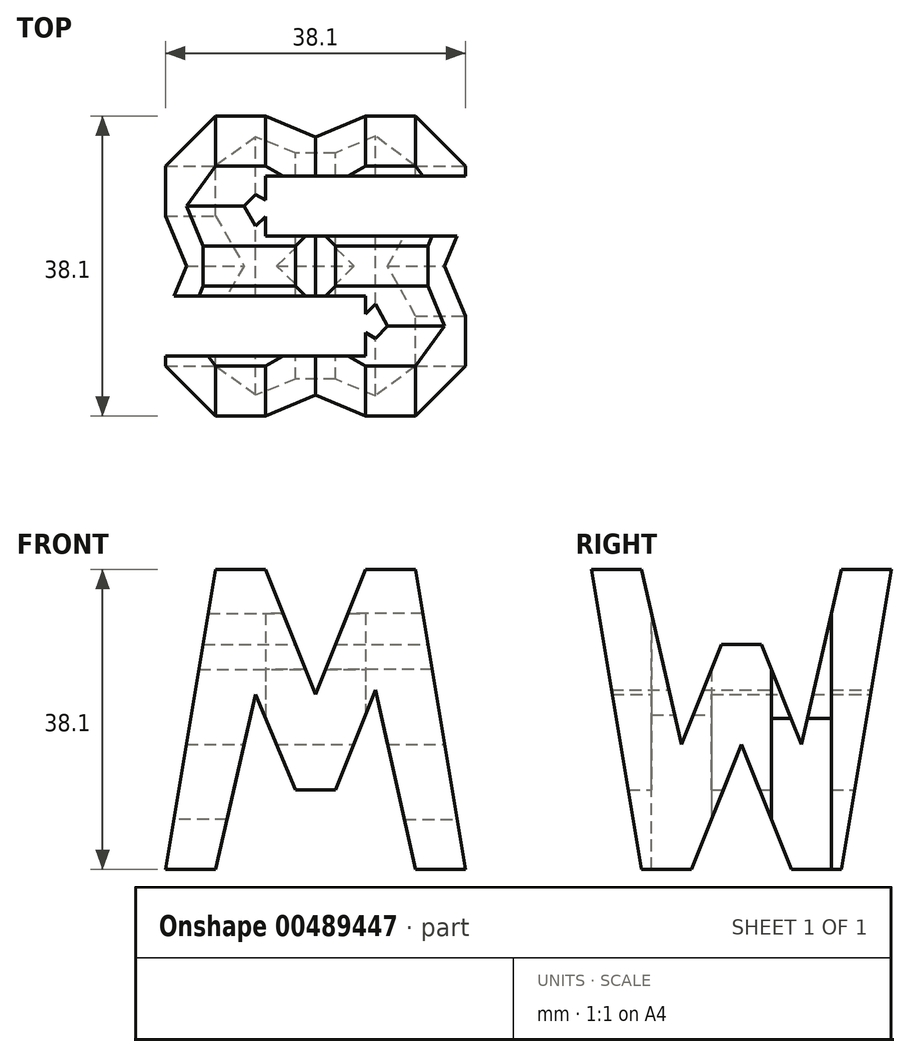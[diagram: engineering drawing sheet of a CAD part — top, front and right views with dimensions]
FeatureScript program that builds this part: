
annotation { "Feature Type Name" : "Feature", "Feature Type Description" : "" }
export const myFeature = defineFeature(function(context is Context, id is Id, definition is map)
    precondition{}
    {
        {
            var Q0;
            Q0=qCreatedBy(makeId("Front.planeOp"),FACE);
            var sketch = newSketch(context, id + "F0", { "sketchPlane" : qUnion([Q0])});
            skLineSegment(sketch, "E0", {"start": v(0, 0) * mm, "end": v(0, 38.1) * mm});
            skLineSegment(sketch, "E1", {"start": v(0, 0) * mm, "end": v(38.1, 0) * mm});
            skLineSegment(sketch, "E2", {"start": v(38.1, 0) * mm, "end": v(38.1, 38.1) * mm});
            skLineSegment(sketch, "E3", {"start": v(0, 38.1) * mm, "end": v(38.1, 38.1) * mm});
            skSolve(sketch);
        }
        {
            var Q0;
            Q0=makeQuery(id+"F0.imprint","IMPRINT",FACE,{"disambiguationData":[TD([[makeQuery(id+"F0.imprint","IMPRINT",EDGE,{"derivedFrom":sQuery(id+"F0.wireOp",EDGE,"E0")}),-1.0]])]});
            extrude(context, id + "F1", {"entities" : qUnion([Q0]), "depth" : 38.1 * mm, "offsetDistance" : 25.4 * mm});
        }
        {
            var Q0;
            Q0=qCreatedBy(makeId("Right.planeOp"),FACE);
            cPlane(context, id + "F2", {"entities" : qUnion([Q0]), "cplaneType" : CPlaneType.OFFSET, "offset" : 38.1 * mm, "width" : 152.4 * mm, "height" : 152.4 * mm});
        }
        {
            var Q0;
            Q0=qCreatedBy(id+"F2.planeOp",FACE);
            var sketch = newSketch(context, id + "F3", { "sketchPlane" : qUnion([Q0])});
            skLineSegment(sketch, "E4", {"start": v(-38.1, 38.1) * mm, "end": v(-38.1, 0) * mm});
            skLineSegment(sketch, "E5", {"start": v(-38.1, 0) * mm, "end": v(0, 0) * mm});
            skLineSegment(sketch, "E6", {"start": v(0, 0) * mm, "end": v(0, 38.1) * mm});
            skLineSegment(sketch, "E7", {"start": v(-38.1, 38.1) * mm, "end": v(0, 38.1) * mm});
            skLineSegment(sketch, "E8", {"start": v(-31.75, 38.1) * mm, "end": v(-26.67, 15.87) * mm});
            skLineSegment(sketch, "E9", {"start": v(-21.59, 28.58) * mm, "end": v(-16.5, 28.58) * mm});
            skLineSegment(sketch, "E10", {"start": v(-25.4, 0) * mm, "end": v(-19.05, 15.88) * mm});
            skLineSegment(sketch, "E11", {"start": v(-19.05, 15.88) * mm, "end": v(-12.7, 0) * mm});
            skLineSegment(sketch, "E12", {"start": v(-11.43, 15.88) * mm, "end": v(-6.35, 38.1) * mm});
            skLineSegment(sketch, "E13", {"start": v(-6.35, 0) * mm, "end": v(0, 38.1) * mm});
            skLineSegment(sketch, "E14", {"start": v(-31.75, 0) * mm, "end": v(-38.1, 38.1) * mm});
            skLineSegment(sketch, "E15", {"start": v(-11.43, 15.88) * mm, "end": v(-16.5, 28.58) * mm});
            skLineSegment(sketch, "E16", {"start": v(-21.59, 28.58) * mm, "end": v(-26.67, 15.87) * mm});
            skSolve(sketch);
        }
        {
            var Q0;
            {var subQ1=sQuery(id+"F3.wireOp",EDGE,"E8");Q0=makeQuery(id+"F3.imprint","IMPRINT",FACE,{"disambiguationData":[TD([[makeQuery(id+"F3.imprint","IMPRINT",EDGE,{"derivedFrom":subQ1}),1.0]])]});}
            var Q1;
            {var subQ0=sQuery(id+"F3.wireOp",EDGE,"E10");Q1=makeQuery(id+"F3.imprint","IMPRINT",FACE,{"disambiguationData":[TD([[makeQuery(id+"F3.imprint","IMPRINT",EDGE,{"derivedFrom":subQ0}),-1.0]])]});}
            var Q2;
            {var subQ0=sQuery(id+"F3.wireOp",EDGE,"E6");Q2=makeQuery(id+"F3.imprint","IMPRINT",FACE,{"disambiguationData":[TD([[makeQuery(id+"F3.imprint","IMPRINT",EDGE,{"derivedFrom":subQ0}),1.0]])]});}
            var Q3;
            {var subQ0=sQuery(id+"F3.wireOp",EDGE,"E4");Q3=makeQuery(id+"F3.imprint","IMPRINT",FACE,{"disambiguationData":[TD([[makeQuery(id+"F3.imprint","IMPRINT",EDGE,{"derivedFrom":subQ0}),1.0]])]});}
            extrude(context, id + "F4", {"entities" : qUnion([Q0, Q1, Q2, Q3]), "operationType" : NewBodyOperationType.REMOVE, "oppositeDirection" : true, "depth" : 38.1 * mm, "offsetDistance" : 25.4 * mm});
        }
        {
            var Q0;
            Q0=qCreatedBy(makeId("Front.planeOp"),FACE);
            var sketch = newSketch(context, id + "F5", { "sketchPlane" : qUnion([Q0])});
            skLineSegment(sketch, "E17", {"start": v(38.1, 38.1) * mm, "end": v(38.1, 0) * mm});
            skLineSegment(sketch, "E18", {"start": v(0, 0) * mm, "end": v(0, 38.1) * mm});
            skLineSegment(sketch, "E19", {"start": v(0, 0) * mm, "end": v(38.1, 0) * mm});
            skLineSegment(sketch, "E20", {"start": v(38.1, 38.1) * mm, "end": v(0, 38.1) * mm});
            skLineSegment(sketch, "E21", {"start": v(38.1, 0) * mm, "end": v(31.75, 38.1) * mm});
            skLineSegment(sketch, "E22", {"start": v(25.4, 38.1) * mm, "end": v(19.05, 22.23) * mm});
            skLineSegment(sketch, "E23", {"start": v(19.05, 22.23) * mm, "end": v(12.7, 38.1) * mm});
            skLineSegment(sketch, "E24", {"start": v(6.35, 38.1) * mm, "end": v(0, 0) * mm});
            skLineSegment(sketch, "E25", {"start": v(31.75, 0) * mm, "end": v(26.67, 22.78) * mm});
            skLineSegment(sketch, "E26", {"start": v(26.67, 22.78) * mm, "end": v(21.59, 10.08) * mm});
            skLineSegment(sketch, "E27", {"start": v(21.59, 10.08) * mm, "end": v(16.51, 10.08) * mm});
            skLineSegment(sketch, "E28", {"start": v(16.51, 10.08) * mm, "end": v(11.43, 22.23) * mm});
            skLineSegment(sketch, "E29", {"start": v(11.43, 22.23) * mm, "end": v(6.35, 0) * mm});
            skSolve(sketch);
        }
        {
            var Q0;
            {var subQ0=sQuery(id+"F5.wireOp",EDGE,"E17");Q0=makeQuery(id+"F5.imprint","IMPRINT",FACE,{"disambiguationData":[TD([[makeQuery(id+"F5.imprint","IMPRINT",EDGE,{"derivedFrom":subQ0}),-1.0]])]});}
            var Q1;
            {var subQ0=sQuery(id+"F5.wireOp",EDGE,"E25");Q1=makeQuery(id+"F5.imprint","IMPRINT",FACE,{"disambiguationData":[TD([[makeQuery(id+"F5.imprint","IMPRINT",EDGE,{"derivedFrom":subQ0}),1.0]])]});}
            var Q2;
            {var subQ0=sQuery(id+"F5.wireOp",EDGE,"E22");Q2=makeQuery(id+"F5.imprint","IMPRINT",FACE,{"disambiguationData":[TD([[makeQuery(id+"F5.imprint","IMPRINT",EDGE,{"derivedFrom":subQ0}),-1.0]])]});}
            var Q3;
            {var subQ0=sQuery(id+"F5.wireOp",EDGE,"E18");Q3=makeQuery(id+"F5.imprint","IMPRINT",FACE,{"disambiguationData":[TD([[makeQuery(id+"F5.imprint","IMPRINT",EDGE,{"derivedFrom":subQ0}),-1.0]])]});}
            extrude(context, id + "F6", {"entities" : qUnion([Q0, Q1, Q2, Q3]), "operationType" : NewBodyOperationType.REMOVE, "depth" : 38.1 * mm, "offsetDistance" : 25.4 * mm});
        }
        {
            var Q0;
            Q0=qCreatedBy(makeId("Top.planeOp"),FACE);
            var sketch = newSketch(context, id + "F7", { "sketchPlane" : qUnion([Q0])});
            skLineSegment(sketch, "E30", {"start": v(0, 0) * mm, "end": v(38.1, 0) * mm});
            skLineSegment(sketch, "E31", {"start": v(38.1, 0) * mm, "end": v(38.1, -38.1) * mm});
            skLineSegment(sketch, "E32", {"start": v(38.1, -38.1) * mm, "end": v(0, -38.1) * mm});
            skLineSegment(sketch, "E33", {"start": v(0, -38.1) * mm, "end": v(0, 0) * mm});
            skLineSegment(sketch, "E34", {"start": v(38.1, -7.62) * mm, "end": v(12.7, -7.62) * mm});
            skLineSegment(sketch, "E35", {"start": v(12.7, -7.62) * mm, "end": v(12.7, -15.24) * mm});
            skLineSegment(sketch, "E36", {"start": v(12.7, -15.24) * mm, "end": v(38.1, -15.24) * mm});
            skLineSegment(sketch, "E37", {"start": v(0, -30.48) * mm, "end": v(25.4, -30.48) * mm});
            skLineSegment(sketch, "E38", {"start": v(25.4, -30.48) * mm, "end": v(25.4, -22.86) * mm});
            skLineSegment(sketch, "E39", {"start": v(25.4, -22.86) * mm, "end": v(0, -22.86) * mm});
            skLineSegment(sketch, "E40", {"start": v(38.1, -15.24) * mm, "end": v(38.1, -7.62) * mm});
            skLineSegment(sketch, "E41", {"start": v(0, -30.48) * mm, "end": v(0, -22.86) * mm});
            skLineSegment(sketch, "E42", {"start": v(0, -38.1) * mm, "end": v(38.1, -38.1) * mm});
            skLineSegment(sketch, "E43", {"start": v(0, 0) * mm, "end": v(0, -38.1) * mm});
            skSolve(sketch);
        }
        {
            var Q0;
            {var subQ0=sQuery(id+"F7.wireOp",EDGE,"E34");Q0=makeQuery(id+"F7.imprint","IMPRINT",FACE,{"disambiguationData":[TD([[makeQuery(id+"F7.imprint","IMPRINT",EDGE,{"derivedFrom":subQ0}),1.0]])]});}
            var Q1;
            {var subQ0=sQuery(id+"F7.wireOp",EDGE,"E37");Q1=makeQuery(id+"F7.imprint","IMPRINT",FACE,{"disambiguationData":[TD([[makeQuery(id+"F7.imprint","IMPRINT",EDGE,{"derivedFrom":subQ0}),1.0]])]});}
            extrude(context, id + "F8", {"entities" : qUnion([Q0, Q1]), "operationType" : NewBodyOperationType.REMOVE, "depth" : 38.1 * mm, "offsetDistance" : 25.4 * mm});
        }
    });
